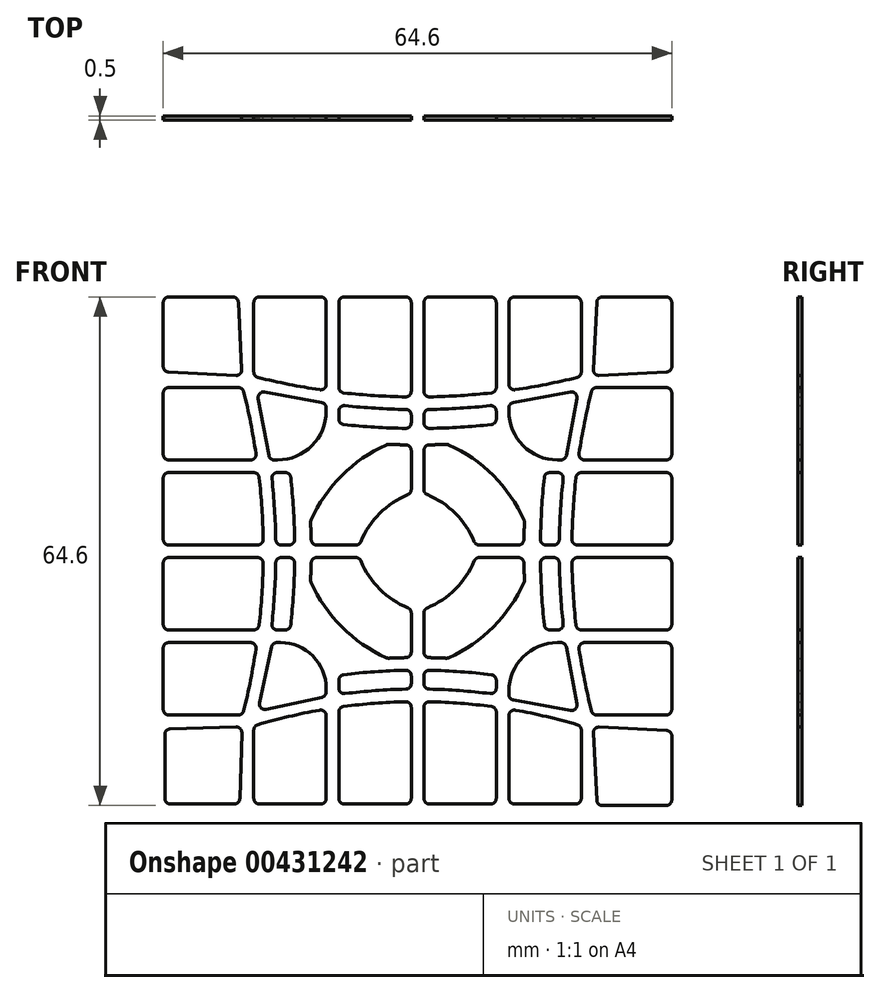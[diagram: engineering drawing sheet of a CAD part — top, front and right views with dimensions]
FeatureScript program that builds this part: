
annotation { "Feature Type Name" : "Feature", "Feature Type Description" : "" }
export const myFeature = defineFeature(function(context is Context, id is Id, definition is map)
    precondition{}
    {
        {
            var Q0;
            Q0=qCreatedBy(makeId("Front.planeOp"),FACE);
            var sketch = newSketch(context, id + "F0", { "sketchPlane" : qUnion([Q0])});
            skLineSegment(sketch, "E0.bottom", {"start": v(33.8, 33.8) * mm, "end": v(-33.8, 33.8) * mm, "construction": true});
            skLineSegment(sketch, "E0.top", {"start": v(33.8, -33.8) * mm, "end": v(-33.8, -33.8) * mm, "construction": true});
            skLineSegment(sketch, "E0.left", {"start": v(33.8, 33.8) * mm, "end": v(33.8, -33.8) * mm, "construction": true});
            skLineSegment(sketch, "E0.right", {"start": v(-33.8, 33.8) * mm, "end": v(-33.8, -33.8) * mm, "construction": true});
            skPoint(sketch, "E0.middle", {"position": v(0, 0) * mm});
            skLineSegment(sketch, "E1", {"start": v(0, 33.8) * mm, "end": v(0, -33.8) * mm, "construction": true});
            skLineSegment(sketch, "E2", {"start": v(-10.8, 33.8) * mm, "end": v(-10.8, -33.8) * mm, "construction": true});
            skLineSegment(sketch, "E3", {"start": v(-21.6, 33.8) * mm, "end": v(-21.6, -33.8) * mm, "construction": true});
            skLineSegment(sketch, "E4", {"start": v(-33.8, 0) * mm, "end": v(33.8, 0) * mm, "construction": true});
            skLineSegment(sketch, "E5", {"start": v(-33.8, -10.8) * mm, "end": v(33.8, -10.8) * mm, "construction": true});
            skLineSegment(sketch, "E6", {"start": v(-33.8, -21.6) * mm, "end": v(33.8, -21.6) * mm, "construction": true});
            skLineSegment(sketch, "E7", {"start": v(-33.8, -33.8) * mm, "end": v(0, 0) * mm});
            skLineSegment(sketch, "E8", {"start": v(-21.6, -33.8) * mm, "end": v(-21.2, -21.2) * mm, "construction": true});
            skLineSegment(sketch, "E9", {"start": v(-21.2, -21.2) * mm, "end": v(-33.8, -21.6) * mm, "construction": true});
            skLineSegment(sketch, "E10", {"start": v(-32.1, -31.4) * mm, "end": v(-32.1, -23.28) * mm});
            skLineSegment(sketch, "E11", {"start": v(-31.42, -22.58) * mm, "end": v(-23.04, -22.32) * mm});
            skLineSegment(sketch, "E12", {"start": v(-22.32, -23.04) * mm, "end": v(-22.58, -31.42) * mm});
            skLineSegment(sketch, "E13", {"start": v(-23.28, -32.1) * mm, "end": v(-31.4, -32.1) * mm});
            skPoint(sketch, "E14.visualSharp", {"position": v(-32.1, -22.6) * mm});
            skArc(sketch, "E14.filletArc", {"start": v(-31.42, -22.58) * mm, "mid": v(-31.9, -22.8) * mm, "end": v(-32.1, -23.28) * mm});
            skPoint(sketch, "E15.visualSharp", {"position": v(-22.3, -22.3) * mm});
            skArc(sketch, "E15.filletArc", {"start": v(-22.32, -23.04) * mm, "mid": v(-22.53, -22.53) * mm, "end": v(-23.04, -22.32) * mm});
            skPoint(sketch, "E16.visualSharp", {"position": v(-22.6, -32.1) * mm});
            skArc(sketch, "E16.filletArc", {"start": v(-23.28, -32.1) * mm, "mid": v(-22.8, -31.9) * mm, "end": v(-22.58, -31.42) * mm});
            skPoint(sketch, "E17.visualSharp", {"position": v(-32.1, -32.1) * mm});
            skArc(sketch, "E17.filletArc", {"start": v(-32.1, -31.4) * mm, "mid": v(-31.9, -31.9) * mm, "end": v(-31.4, -32.1) * mm});
            skLineSegment(sketch, "E18.MirrorCS", {"start": v(21.6, -33.8) * mm, "end": v(21.2, -21.2) * mm, "construction": true});
            skLineSegment(sketch, "E19", {"start": v(-20.8, -22.71) * mm, "end": v(-20.8, -31.4) * mm});
            skLineSegment(sketch, "E20", {"start": v(-20.1, -32.1) * mm, "end": v(-12.3, -32.1) * mm});
            skLineSegment(sketch, "E21", {"start": v(-11.6, -31.4) * mm, "end": v(-11.6, -20.88) * mm});
            skLineSegment(sketch, "E22", {"start": v(-10, -20.41) * mm, "end": v(-10, -31.4) * mm});
            skLineSegment(sketch, "E23", {"start": v(-9.3, -32.1) * mm, "end": v(-1.5, -32.1) * mm});
            skLineSegment(sketch, "E24", {"start": v(-0.8, -31.4) * mm, "end": v(-0.8, -19.82) * mm});
            skArc(sketch, "E25.trimOffspring", {"start": v(-12.42, -20.19) * mm, "mid": v(-16.39, -21) * mm, "end": v(-20.3, -22.04) * mm});
            skArc(sketch, "E26.trimOffspring", {"start": v(-1.51, -19.12) * mm, "mid": v(-5.46, -19.3) * mm, "end": v(-9.4, -19.72) * mm});
            skPoint(sketch, "E27.visualSharp", {"position": v(-20.8, -22.2) * mm});
            skArc(sketch, "E27.filletArc", {"start": v(-20.3, -22.04) * mm, "mid": v(-20.66, -22.3) * mm, "end": v(-20.8, -22.71) * mm});
            skPoint(sketch, "E28.visualSharp", {"position": v(-11.6, -20.05) * mm});
            skArc(sketch, "E28.filletArc", {"start": v(-11.6, -20.88) * mm, "mid": v(-11.85, -20.34) * mm, "end": v(-12.42, -20.19) * mm});
            skPoint(sketch, "E29.visualSharp", {"position": v(-11.6, -32.1) * mm});
            skArc(sketch, "E29.filletArc", {"start": v(-12.3, -32.1) * mm, "mid": v(-11.8, -31.9) * mm, "end": v(-11.6, -31.4) * mm});
            skPoint(sketch, "E30.visualSharp", {"position": v(-20.8, -32.1) * mm});
            skArc(sketch, "E30.filletArc", {"start": v(-20.8, -31.4) * mm, "mid": v(-20.6, -31.9) * mm, "end": v(-20.1, -32.1) * mm});
            skPoint(sketch, "E31.visualSharp", {"position": v(-10, -32.1) * mm});
            skArc(sketch, "E31.filletArc", {"start": v(-10, -31.4) * mm, "mid": v(-9.8, -31.9) * mm, "end": v(-9.3, -32.1) * mm});
            skPoint(sketch, "E32.visualSharp", {"position": v(-0.8, -32.1) * mm});
            skArc(sketch, "E32.filletArc", {"start": v(-1.5, -32.1) * mm, "mid": v(-1, -31.9) * mm, "end": v(-0.8, -31.4) * mm});
            skPoint(sketch, "E33.visualSharp", {"position": v(-0.8, -19.1) * mm});
            skArc(sketch, "E33.filletArc", {"start": v(-0.8, -19.82) * mm, "mid": v(-1.01, -19.32) * mm, "end": v(-1.51, -19.12) * mm});
            skPoint(sketch, "E34.visualSharp", {"position": v(-10, -19.8) * mm});
            skArc(sketch, "E34.filletArc", {"start": v(-9.4, -19.72) * mm, "mid": v(-9.83, -19.95) * mm, "end": v(-10, -20.41) * mm});
            skArc(sketch, "E35.0", {"start": v(17.07, -16.23) * mm, "mid": v(0, -14.3) * mm, "end": v(-17.07, -16.23) * mm, "construction": true});
            skLineSegment(sketch, "E36", {"start": v(-10, -17.39) * mm, "end": v(-10, -16.38) * mm});
            skLineSegment(sketch, "E37", {"start": v(-0.8, -15.82) * mm, "end": v(-0.8, -16.82) * mm});
            skArc(sketch, "E38", {"start": v(-1.51, -15.12) * mm, "mid": v(-5.46, -15.3) * mm, "end": v(-9.39, -15.69) * mm});
            skArc(sketch, "E39", {"start": v(-1.49, -17.52) * mm, "mid": v(-5.36, -17.7) * mm, "end": v(-9.21, -18.08) * mm});
            skPoint(sketch, "E40.visualSharp", {"position": v(-10, -18.19) * mm});
            skArc(sketch, "E40.filletArc", {"start": v(-10, -17.39) * mm, "mid": v(-9.76, -17.91) * mm, "end": v(-9.21, -18.08) * mm});
            skPoint(sketch, "E41.visualSharp", {"position": v(-10, -15.76) * mm});
            skArc(sketch, "E41.filletArc", {"start": v(-9.39, -15.69) * mm, "mid": v(-9.82, -15.92) * mm, "end": v(-10, -16.38) * mm});
            skPoint(sketch, "E42.visualSharp", {"position": v(-0.8, -15.1) * mm});
            skArc(sketch, "E42.filletArc", {"start": v(-0.8, -15.82) * mm, "mid": v(-1.01, -15.32) * mm, "end": v(-1.51, -15.12) * mm});
            skPoint(sketch, "E43.visualSharp", {"position": v(-0.8, -17.5) * mm});
            skArc(sketch, "E43.filletArc", {"start": v(-1.49, -17.52) * mm, "mid": v(-1, -17.3) * mm, "end": v(-0.8, -16.82) * mm});
            skLineSegment(sketch, "E44", {"start": v(-19.25, -20.08) * mm, "end": v(-12.15, -18.55) * mm});
            skLineSegment(sketch, "E45.MirrorCS", {"start": v(-20.08, -19.25) * mm, "end": v(-18.55, -12.15) * mm});
            skLineSegment(sketch, "E46", {"start": v(-11.6, -17.86) * mm, "end": v(-11.6, -17.43) * mm});
            skLineSegment(sketch, "E47.MirrorCS", {"start": v(-17.86, -11.6) * mm, "end": v(-17.43, -11.6) * mm});
            skArc(sketch, "E48", {"start": v(-11.6, -17.43) * mm, "mid": v(-13.3, -13.3) * mm, "end": v(-17.43, -11.6) * mm});
            skPoint(sketch, "E49.visualSharp", {"position": v(-18.43, -11.6) * mm});
            skArc(sketch, "E49.filletArc", {"start": v(-17.86, -11.6) * mm, "mid": v(-18.3, -11.76) * mm, "end": v(-18.55, -12.15) * mm});
            skPoint(sketch, "E50.visualSharp", {"position": v(-20.3, -20.3) * mm});
            skArc(sketch, "E50.filletArc", {"start": v(-20.08, -19.25) * mm, "mid": v(-19.89, -19.89) * mm, "end": v(-19.25, -20.08) * mm});
            skPoint(sketch, "E51.visualSharp", {"position": v(-11.6, -18.43) * mm});
            skArc(sketch, "E51.filletArc", {"start": v(-12.15, -18.55) * mm, "mid": v(-11.76, -18.3) * mm, "end": v(-11.6, -17.86) * mm});
            skCircle(sketch, "E52", {"center": v(0, 0) * mm, "radius": 6 * mm, "construction": true});
            skLineSegment(sketch, "E53", {"start": v(-0.8, -12.81) * mm, "end": v(-0.8, -7.84) * mm});
            skArc(sketch, "E54", {"start": v(-1.49, -13.51) * mm, "mid": v(-2.56, -13.54) * mm, "end": v(-3.63, -13.59) * mm});
            skArc(sketch, "E55.MirrorCS", {"start": v(-13.51, -1.49) * mm, "mid": v(-13.54, -2.56) * mm, "end": v(-13.59, -3.63) * mm});
            skLineSegment(sketch, "E56.MirrorCS", {"start": v(-12.81, -0.8) * mm, "end": v(-7.84, -0.8) * mm});
            skPoint(sketch, "E57.visualSharp", {"position": v(-13.6, -3.8) * mm});
            skPoint(sketch, "E58.visualSharp", {"position": v(-13.5, -0.8) * mm});
            skArc(sketch, "E58.filletArc", {"start": v(-12.81, -0.8) * mm, "mid": v(-13.3, -1) * mm, "end": v(-13.51, -1.49) * mm});
            skPoint(sketch, "E59.visualSharp", {"position": v(-7.36, -0.8) * mm});
            skPoint(sketch, "E60.visualSharp", {"position": v(-0.8, -7.36) * mm});
            skPoint(sketch, "E61.visualSharp", {"position": v(-0.8, -13.5) * mm});
            skArc(sketch, "E61.filletArc", {"start": v(-1.49, -13.51) * mm, "mid": v(-1, -13.3) * mm, "end": v(-0.8, -12.81) * mm});
            skPoint(sketch, "E62.visualSharp", {"position": v(-3.8, -13.6) * mm});
            skPoint(sketch, "E63.visualSharp", {"position": v(-9.62, -9.62) * mm});
            skLineSegment(sketch, "E64.MirrorCS", {"start": v(0.8, -31.4) * mm, "end": v(0.8, -19.82) * mm});
            skArc(sketch, "E65.MirrorCS", {"start": v(1.5, -32.1) * mm, "mid": v(1, -31.9) * mm, "end": v(0.8, -31.4) * mm});
            skLineSegment(sketch, "E66.MirrorCS", {"start": v(9.3, -32.1) * mm, "end": v(1.5, -32.1) * mm});
            skArc(sketch, "E67.MirrorCS", {"start": v(10, -31.4) * mm, "mid": v(9.8, -31.9) * mm, "end": v(9.3, -32.1) * mm});
            skLineSegment(sketch, "E68.MirrorCS", {"start": v(10, -20.41) * mm, "end": v(10, -31.4) * mm});
            skArc(sketch, "E69.MirrorCS", {"start": v(9.4, -19.72) * mm, "mid": v(9.83, -19.95) * mm, "end": v(10, -20.41) * mm});
            skArc(sketch, "E70.MirrorCS", {"start": v(1.51, -19.12) * mm, "mid": v(5.46, -19.3) * mm, "end": v(9.4, -19.72) * mm});
            skArc(sketch, "E71.MirrorCS", {"start": v(0.8, -19.82) * mm, "mid": v(1.01, -19.32) * mm, "end": v(1.51, -19.12) * mm});
            skArc(sketch, "E72.MirrorCS", {"start": v(11.6, -20.88) * mm, "mid": v(11.85, -20.34) * mm, "end": v(12.42, -20.19) * mm});
            skLineSegment(sketch, "E73.MirrorCS", {"start": v(11.6, -31.4) * mm, "end": v(11.6, -20.88) * mm});
            skArc(sketch, "E74.MirrorCS", {"start": v(12.3, -32.1) * mm, "mid": v(11.8, -31.9) * mm, "end": v(11.6, -31.4) * mm});
            skLineSegment(sketch, "E75.MirrorCS", {"start": v(20.1, -32.1) * mm, "end": v(12.3, -32.1) * mm});
            skArc(sketch, "E76.MirrorCS", {"start": v(20.8, -31.4) * mm, "mid": v(20.6, -31.9) * mm, "end": v(20.1, -32.1) * mm});
            skLineSegment(sketch, "E77.MirrorCS", {"start": v(20.8, -22.71) * mm, "end": v(20.8, -31.4) * mm});
            skArc(sketch, "E78.MirrorCS", {"start": v(20.3, -22.04) * mm, "mid": v(20.66, -22.3) * mm, "end": v(20.8, -22.71) * mm});
            skArc(sketch, "E79.MirrorCS", {"start": v(12.42, -20.19) * mm, "mid": v(16.39, -21) * mm, "end": v(20.3, -22.04) * mm});
            skArc(sketch, "E80.MirrorCS", {"start": v(1.51, -15.12) * mm, "mid": v(5.46, -15.3) * mm, "end": v(9.39, -15.69) * mm});
            skArc(sketch, "E81.MirrorCS", {"start": v(0.8, -15.82) * mm, "mid": v(1.01, -15.32) * mm, "end": v(1.51, -15.12) * mm});
            skLineSegment(sketch, "E82.MirrorCS", {"start": v(0.8, -15.82) * mm, "end": v(0.8, -16.82) * mm});
            skArc(sketch, "E83.MirrorCS", {"start": v(1.49, -17.52) * mm, "mid": v(1, -17.3) * mm, "end": v(0.8, -16.82) * mm});
            skArc(sketch, "E84.MirrorCS", {"start": v(1.49, -17.52) * mm, "mid": v(5.36, -17.7) * mm, "end": v(9.21, -18.08) * mm});
            skArc(sketch, "E85.MirrorCS", {"start": v(10, -17.39) * mm, "mid": v(9.76, -17.91) * mm, "end": v(9.21, -18.08) * mm});
            skLineSegment(sketch, "E86.MirrorCS", {"start": v(10, -17.39) * mm, "end": v(10, -16.38) * mm});
            skArc(sketch, "E87.MirrorCS", {"start": v(9.39, -15.69) * mm, "mid": v(9.82, -15.92) * mm, "end": v(10, -16.38) * mm});
            skLineSegment(sketch, "E88.1.0", {"start": v(31.6, -32.3) * mm, "end": v(23.47, -32.3) * mm});
            skArc(sketch, "E88.1.1", {"start": v(22.77, -31.63) * mm, "mid": v(22.98, -32.1) * mm, "end": v(23.47, -32.3) * mm});
            skLineSegment(sketch, "E88.1.2", {"start": v(22.77, -31.63) * mm, "end": v(22.34, -23.07) * mm});
            skArc(sketch, "E88.1.3", {"start": v(23.07, -22.34) * mm, "mid": v(22.54, -22.54) * mm, "end": v(22.34, -23.07) * mm});
            skLineSegment(sketch, "E88.1.4", {"start": v(23.07, -22.34) * mm, "end": v(31.63, -22.77) * mm});
            skArc(sketch, "E88.1.5", {"start": v(32.3, -23.47) * mm, "mid": v(32.1, -22.98) * mm, "end": v(31.63, -22.77) * mm});
            skLineSegment(sketch, "E88.1.6", {"start": v(32.3, -23.47) * mm, "end": v(32.3, -31.6) * mm});
            skArc(sketch, "E88.1.7", {"start": v(31.6, -32.3) * mm, "mid": v(32.1, -32.1) * mm, "end": v(32.3, -31.6) * mm});
            skLineSegment(sketch, "E88.1.8", {"start": v(22.76, -20.8) * mm, "end": v(31.6, -20.8) * mm});
            skArc(sketch, "E88.1.9", {"start": v(22.08, -20.27) * mm, "mid": v(22.33, -20.65) * mm, "end": v(22.76, -20.8) * mm});
            skArc(sketch, "E88.1.10", {"start": v(20.52, -12.4) * mm, "mid": v(21.2, -16.35) * mm, "end": v(22.08, -20.27) * mm});
            skArc(sketch, "E88.1.11", {"start": v(21.21, -11.6) * mm, "mid": v(20.68, -11.84) * mm, "end": v(20.52, -12.4) * mm});
            skLineSegment(sketch, "E88.1.12", {"start": v(31.6, -11.6) * mm, "end": v(21.21, -11.6) * mm});
            skArc(sketch, "E88.1.13", {"start": v(32.3, -12.3) * mm, "mid": v(32.1, -11.8) * mm, "end": v(31.6, -11.6) * mm});
            skLineSegment(sketch, "E88.1.14", {"start": v(32.3, -20.1) * mm, "end": v(32.3, -12.3) * mm});
            skArc(sketch, "E88.1.15", {"start": v(31.6, -20.8) * mm, "mid": v(32.1, -20.6) * mm, "end": v(32.3, -20.1) * mm});
            skArc(sketch, "E88.1.16", {"start": v(31.6, -10) * mm, "mid": v(32.1, -9.8) * mm, "end": v(32.3, -9.3) * mm});
            skLineSegment(sketch, "E88.1.17", {"start": v(20.82, -10) * mm, "end": v(31.6, -10) * mm});
            skArc(sketch, "E88.1.18", {"start": v(20.13, -9.38) * mm, "mid": v(20.35, -9.82) * mm, "end": v(20.82, -10) * mm});
            skArc(sketch, "E88.1.19", {"start": v(19.61, -1.51) * mm, "mid": v(19.78, -5.45) * mm, "end": v(20.13, -9.38) * mm});
            skArc(sketch, "E88.1.20", {"start": v(20.31, -0.8) * mm, "mid": v(19.81, -1) * mm, "end": v(19.61, -1.51) * mm});
            skLineSegment(sketch, "E88.1.21", {"start": v(31.6, -0.8) * mm, "end": v(20.31, -0.8) * mm});
            skArc(sketch, "E88.1.22", {"start": v(32.3, -1.5) * mm, "mid": v(32.1, -1) * mm, "end": v(31.6, -0.8) * mm});
            skLineSegment(sketch, "E88.1.23", {"start": v(32.3, -9.3) * mm, "end": v(32.3, -1.5) * mm});
            skArc(sketch, "E88.1.24", {"start": v(32.3, 1.5) * mm, "mid": v(32.1, 1) * mm, "end": v(31.6, 0.8) * mm});
            skLineSegment(sketch, "E88.1.25", {"start": v(32.3, 9.3) * mm, "end": v(32.3, 1.5) * mm});
            skArc(sketch, "E88.1.26", {"start": v(31.6, 10) * mm, "mid": v(32.1, 9.8) * mm, "end": v(32.3, 9.3) * mm});
            skLineSegment(sketch, "E88.1.27", {"start": v(20.82, 10) * mm, "end": v(31.6, 10) * mm});
            skArc(sketch, "E88.1.28", {"start": v(20.13, 9.38) * mm, "mid": v(20.35, 9.82) * mm, "end": v(20.82, 10) * mm});
            skArc(sketch, "E88.1.29", {"start": v(19.61, 1.51) * mm, "mid": v(19.78, 5.45) * mm, "end": v(20.13, 9.38) * mm});
            skArc(sketch, "E88.1.30", {"start": v(20.31, 0.8) * mm, "mid": v(19.81, 1) * mm, "end": v(19.61, 1.51) * mm});
            skLineSegment(sketch, "E88.1.31", {"start": v(31.6, 0.8) * mm, "end": v(20.31, 0.8) * mm});
            skArc(sketch, "E88.1.32", {"start": v(32.3, 12.3) * mm, "mid": v(32.1, 11.8) * mm, "end": v(31.6, 11.6) * mm});
            skLineSegment(sketch, "E88.1.33", {"start": v(32.3, 20.1) * mm, "end": v(32.3, 12.3) * mm});
            skArc(sketch, "E88.1.34", {"start": v(31.6, 20.8) * mm, "mid": v(32.1, 20.6) * mm, "end": v(32.3, 20.1) * mm});
            skLineSegment(sketch, "E88.1.35", {"start": v(22.76, 20.8) * mm, "end": v(31.6, 20.8) * mm});
            skArc(sketch, "E88.1.36", {"start": v(22.08, 20.27) * mm, "mid": v(22.33, 20.65) * mm, "end": v(22.76, 20.8) * mm});
            skArc(sketch, "E88.1.37", {"start": v(20.52, 12.4) * mm, "mid": v(21.2, 16.35) * mm, "end": v(22.08, 20.27) * mm});
            skArc(sketch, "E88.1.38", {"start": v(21.21, 11.6) * mm, "mid": v(20.68, 11.84) * mm, "end": v(20.52, 12.4) * mm});
            skLineSegment(sketch, "E88.1.39", {"start": v(31.6, 11.6) * mm, "end": v(21.21, 11.6) * mm});
            skArc(sketch, "E88.1.40", {"start": v(17.8, 10) * mm, "mid": v(18.32, 9.77) * mm, "end": v(18.5, 9.22) * mm});
            skArc(sketch, "E88.1.41", {"start": v(18.01, 1.49) * mm, "mid": v(18.17, 5.36) * mm, "end": v(18.5, 9.22) * mm});
            skArc(sketch, "E88.1.42", {"start": v(18.01, 1.49) * mm, "mid": v(17.8, 1) * mm, "end": v(17.31, 0.8) * mm});
            skLineSegment(sketch, "E88.1.43", {"start": v(16.31, 0.8) * mm, "end": v(17.31, 0.8) * mm});
            skArc(sketch, "E88.1.44", {"start": v(16.31, 0.8) * mm, "mid": v(15.81, 1) * mm, "end": v(15.61, 1.51) * mm});
            skArc(sketch, "E88.1.45", {"start": v(15.61, 1.51) * mm, "mid": v(15.77, 5.45) * mm, "end": v(16.1, 9.37) * mm});
            skArc(sketch, "E88.1.46", {"start": v(16.1, 9.37) * mm, "mid": v(16.33, 9.82) * mm, "end": v(16.8, 10) * mm});
            skLineSegment(sketch, "E88.1.47", {"start": v(17.8, 10) * mm, "end": v(16.8, 10) * mm});
            skArc(sketch, "E88.1.48", {"start": v(16.31, -0.8) * mm, "mid": v(15.81, -1) * mm, "end": v(15.61, -1.51) * mm});
            skArc(sketch, "E88.1.49", {"start": v(15.61, -1.51) * mm, "mid": v(15.77, -5.45) * mm, "end": v(16.1, -9.37) * mm});
            skLineSegment(sketch, "E88.1.50", {"start": v(16.31, -0.8) * mm, "end": v(17.31, -0.8) * mm});
            skArc(sketch, "E88.1.51", {"start": v(18.01, -1.49) * mm, "mid": v(17.8, -1) * mm, "end": v(17.31, -0.8) * mm});
            skArc(sketch, "E88.1.52", {"start": v(18.01, -1.49) * mm, "mid": v(18.17, -5.36) * mm, "end": v(18.5, -9.22) * mm});
            skArc(sketch, "E88.1.53", {"start": v(17.8, -10) * mm, "mid": v(18.32, -9.77) * mm, "end": v(18.5, -9.22) * mm});
            skLineSegment(sketch, "E88.1.54", {"start": v(17.8, -10) * mm, "end": v(16.8, -10) * mm});
            skArc(sketch, "E88.1.55", {"start": v(16.1, -9.37) * mm, "mid": v(16.33, -9.82) * mm, "end": v(16.8, -10) * mm});
            skArc(sketch, "E88.1.56", {"start": v(17.8, -11.6) * mm, "mid": v(13.41, -13.41) * mm, "end": v(11.6, -17.8) * mm});
            skLineSegment(sketch, "E88.1.57", {"start": v(18.2, -11.6) * mm, "end": v(17.8, -11.6) * mm});
            skArc(sketch, "E88.1.58", {"start": v(18.9, -12.17) * mm, "mid": v(18.66, -11.76) * mm, "end": v(18.2, -11.6) * mm});
            skLineSegment(sketch, "E88.1.59", {"start": v(20.23, -19.42) * mm, "end": v(18.9, -12.17) * mm});
            skArc(sketch, "E88.1.60", {"start": v(19.42, -20.23) * mm, "mid": v(20.04, -20.04) * mm, "end": v(20.23, -19.42) * mm});
            skLineSegment(sketch, "E88.1.61", {"start": v(19.42, -20.23) * mm, "end": v(12.17, -18.9) * mm});
            skArc(sketch, "E88.1.62", {"start": v(11.6, -18.2) * mm, "mid": v(11.76, -18.66) * mm, "end": v(12.17, -18.9) * mm});
            skLineSegment(sketch, "E88.1.63", {"start": v(11.6, -18.2) * mm, "end": v(11.6, -17.8) * mm});
            skLineSegment(sketch, "E88.2.0", {"start": v(32.3, 31.6) * mm, "end": v(32.3, 23.47) * mm});
            skArc(sketch, "E88.2.1", {"start": v(31.63, 22.77) * mm, "mid": v(32.1, 22.98) * mm, "end": v(32.3, 23.47) * mm});
            skLineSegment(sketch, "E88.2.2", {"start": v(31.63, 22.77) * mm, "end": v(23.07, 22.34) * mm});
            skArc(sketch, "E88.2.3", {"start": v(22.34, 23.07) * mm, "mid": v(22.54, 22.54) * mm, "end": v(23.07, 22.34) * mm});
            skLineSegment(sketch, "E88.2.4", {"start": v(22.34, 23.07) * mm, "end": v(22.77, 31.63) * mm});
            skArc(sketch, "E88.2.5", {"start": v(23.47, 32.3) * mm, "mid": v(22.98, 32.1) * mm, "end": v(22.77, 31.63) * mm});
            skLineSegment(sketch, "E88.2.6", {"start": v(23.47, 32.3) * mm, "end": v(31.6, 32.3) * mm});
            skArc(sketch, "E88.2.7", {"start": v(32.3, 31.6) * mm, "mid": v(32.1, 32.1) * mm, "end": v(31.6, 32.3) * mm});
            skLineSegment(sketch, "E88.2.8", {"start": v(20.8, 22.76) * mm, "end": v(20.8, 31.6) * mm});
            skArc(sketch, "E88.2.9", {"start": v(20.27, 22.08) * mm, "mid": v(20.65, 22.33) * mm, "end": v(20.8, 22.76) * mm});
            skArc(sketch, "E88.2.10", {"start": v(12.4, 20.52) * mm, "mid": v(16.35, 21.2) * mm, "end": v(20.27, 22.08) * mm});
            skArc(sketch, "E88.2.11", {"start": v(11.6, 21.21) * mm, "mid": v(11.84, 20.68) * mm, "end": v(12.4, 20.52) * mm});
            skLineSegment(sketch, "E88.2.12", {"start": v(11.6, 31.6) * mm, "end": v(11.6, 21.21) * mm});
            skArc(sketch, "E88.2.13", {"start": v(12.3, 32.3) * mm, "mid": v(11.8, 32.1) * mm, "end": v(11.6, 31.6) * mm});
            skLineSegment(sketch, "E88.2.14", {"start": v(20.1, 32.3) * mm, "end": v(12.3, 32.3) * mm});
            skArc(sketch, "E88.2.15", {"start": v(20.8, 31.6) * mm, "mid": v(20.6, 32.1) * mm, "end": v(20.1, 32.3) * mm});
            skArc(sketch, "E88.2.16", {"start": v(10, 31.6) * mm, "mid": v(9.8, 32.1) * mm, "end": v(9.3, 32.3) * mm});
            skLineSegment(sketch, "E88.2.17", {"start": v(10, 20.82) * mm, "end": v(10, 31.6) * mm});
            skArc(sketch, "E88.2.18", {"start": v(9.38, 20.13) * mm, "mid": v(9.82, 20.35) * mm, "end": v(10, 20.82) * mm});
            skArc(sketch, "E88.2.19", {"start": v(1.51, 19.61) * mm, "mid": v(5.45, 19.78) * mm, "end": v(9.38, 20.13) * mm});
            skArc(sketch, "E88.2.20", {"start": v(0.8, 20.31) * mm, "mid": v(1, 19.81) * mm, "end": v(1.51, 19.61) * mm});
            skLineSegment(sketch, "E88.2.21", {"start": v(0.8, 31.6) * mm, "end": v(0.8, 20.31) * mm});
            skArc(sketch, "E88.2.22", {"start": v(1.5, 32.3) * mm, "mid": v(1, 32.1) * mm, "end": v(0.8, 31.6) * mm});
            skLineSegment(sketch, "E88.2.23", {"start": v(9.3, 32.3) * mm, "end": v(1.5, 32.3) * mm});
            skArc(sketch, "E88.2.24", {"start": v(-1.5, 32.3) * mm, "mid": v(-1, 32.1) * mm, "end": v(-0.8, 31.6) * mm});
            skLineSegment(sketch, "E88.2.25", {"start": v(-9.3, 32.3) * mm, "end": v(-1.5, 32.3) * mm});
            skArc(sketch, "E88.2.26", {"start": v(-10, 31.6) * mm, "mid": v(-9.8, 32.1) * mm, "end": v(-9.3, 32.3) * mm});
            skLineSegment(sketch, "E88.2.27", {"start": v(-10, 20.82) * mm, "end": v(-10, 31.6) * mm});
            skArc(sketch, "E88.2.28", {"start": v(-9.38, 20.13) * mm, "mid": v(-9.82, 20.35) * mm, "end": v(-10, 20.82) * mm});
            skArc(sketch, "E88.2.29", {"start": v(-1.51, 19.61) * mm, "mid": v(-5.45, 19.78) * mm, "end": v(-9.38, 20.13) * mm});
            skArc(sketch, "E88.2.30", {"start": v(-0.8, 20.31) * mm, "mid": v(-1, 19.81) * mm, "end": v(-1.51, 19.61) * mm});
            skLineSegment(sketch, "E88.2.31", {"start": v(-0.8, 31.6) * mm, "end": v(-0.8, 20.31) * mm});
            skArc(sketch, "E88.2.32", {"start": v(-12.3, 32.3) * mm, "mid": v(-11.8, 32.1) * mm, "end": v(-11.6, 31.6) * mm});
            skLineSegment(sketch, "E88.2.33", {"start": v(-20.1, 32.3) * mm, "end": v(-12.3, 32.3) * mm});
            skArc(sketch, "E88.2.34", {"start": v(-20.8, 31.6) * mm, "mid": v(-20.6, 32.1) * mm, "end": v(-20.1, 32.3) * mm});
            skLineSegment(sketch, "E88.2.35", {"start": v(-20.8, 22.76) * mm, "end": v(-20.8, 31.6) * mm});
            skArc(sketch, "E88.2.36", {"start": v(-20.27, 22.08) * mm, "mid": v(-20.65, 22.33) * mm, "end": v(-20.8, 22.76) * mm});
            skArc(sketch, "E88.2.37", {"start": v(-12.4, 20.52) * mm, "mid": v(-16.35, 21.2) * mm, "end": v(-20.27, 22.08) * mm});
            skArc(sketch, "E88.2.38", {"start": v(-11.6, 21.21) * mm, "mid": v(-11.84, 20.68) * mm, "end": v(-12.4, 20.52) * mm});
            skLineSegment(sketch, "E88.2.39", {"start": v(-11.6, 31.6) * mm, "end": v(-11.6, 21.21) * mm});
            skArc(sketch, "E88.2.40", {"start": v(-10, 17.8) * mm, "mid": v(-9.77, 18.32) * mm, "end": v(-9.22, 18.5) * mm});
            skArc(sketch, "E88.2.41", {"start": v(-1.49, 18.01) * mm, "mid": v(-5.36, 18.17) * mm, "end": v(-9.22, 18.5) * mm});
            skArc(sketch, "E88.2.42", {"start": v(-1.49, 18.01) * mm, "mid": v(-1, 17.8) * mm, "end": v(-0.8, 17.31) * mm});
            skLineSegment(sketch, "E88.2.43", {"start": v(-0.8, 16.31) * mm, "end": v(-0.8, 17.31) * mm});
            skArc(sketch, "E88.2.44", {"start": v(-0.8, 16.31) * mm, "mid": v(-1, 15.81) * mm, "end": v(-1.51, 15.61) * mm});
            skArc(sketch, "E88.2.45", {"start": v(-1.51, 15.61) * mm, "mid": v(-5.45, 15.77) * mm, "end": v(-9.37, 16.1) * mm});
            skArc(sketch, "E88.2.46", {"start": v(-9.37, 16.1) * mm, "mid": v(-9.82, 16.33) * mm, "end": v(-10, 16.8) * mm});
            skLineSegment(sketch, "E88.2.47", {"start": v(-10, 17.8) * mm, "end": v(-10, 16.8) * mm});
            skArc(sketch, "E88.2.48", {"start": v(0.8, 16.31) * mm, "mid": v(1, 15.81) * mm, "end": v(1.51, 15.61) * mm});
            skArc(sketch, "E88.2.49", {"start": v(1.51, 15.61) * mm, "mid": v(5.45, 15.77) * mm, "end": v(9.37, 16.1) * mm});
            skLineSegment(sketch, "E88.2.50", {"start": v(0.8, 16.31) * mm, "end": v(0.8, 17.31) * mm});
            skArc(sketch, "E88.2.51", {"start": v(1.49, 18.01) * mm, "mid": v(1, 17.8) * mm, "end": v(0.8, 17.31) * mm});
            skArc(sketch, "E88.2.52", {"start": v(1.49, 18.01) * mm, "mid": v(5.36, 18.17) * mm, "end": v(9.22, 18.5) * mm});
            skArc(sketch, "E88.2.53", {"start": v(10, 17.8) * mm, "mid": v(9.77, 18.32) * mm, "end": v(9.22, 18.5) * mm});
            skLineSegment(sketch, "E88.2.54", {"start": v(10, 17.8) * mm, "end": v(10, 16.8) * mm});
            skArc(sketch, "E88.2.55", {"start": v(9.37, 16.1) * mm, "mid": v(9.82, 16.33) * mm, "end": v(10, 16.8) * mm});
            skArc(sketch, "E88.2.56", {"start": v(11.6, 17.8) * mm, "mid": v(13.41, 13.41) * mm, "end": v(17.8, 11.6) * mm});
            skLineSegment(sketch, "E88.2.57", {"start": v(11.6, 18.2) * mm, "end": v(11.6, 17.8) * mm});
            skArc(sketch, "E88.2.58", {"start": v(12.17, 18.9) * mm, "mid": v(11.76, 18.66) * mm, "end": v(11.6, 18.2) * mm});
            skLineSegment(sketch, "E88.2.59", {"start": v(19.42, 20.23) * mm, "end": v(12.17, 18.9) * mm});
            skArc(sketch, "E88.2.60", {"start": v(20.23, 19.42) * mm, "mid": v(20.04, 20.04) * mm, "end": v(19.42, 20.23) * mm});
            skLineSegment(sketch, "E88.2.61", {"start": v(20.23, 19.42) * mm, "end": v(18.9, 12.17) * mm});
            skArc(sketch, "E88.2.62", {"start": v(18.2, 11.6) * mm, "mid": v(18.66, 11.76) * mm, "end": v(18.9, 12.17) * mm});
            skLineSegment(sketch, "E88.2.63", {"start": v(18.2, 11.6) * mm, "end": v(17.8, 11.6) * mm});
            skLineSegment(sketch, "E88.3.0", {"start": v(-31.6, 32.3) * mm, "end": v(-23.47, 32.3) * mm});
            skArc(sketch, "E88.3.1", {"start": v(-22.77, 31.63) * mm, "mid": v(-22.98, 32.1) * mm, "end": v(-23.47, 32.3) * mm});
            skLineSegment(sketch, "E88.3.2", {"start": v(-22.77, 31.63) * mm, "end": v(-22.34, 23.07) * mm});
            skArc(sketch, "E88.3.3", {"start": v(-23.07, 22.34) * mm, "mid": v(-22.54, 22.54) * mm, "end": v(-22.34, 23.07) * mm});
            skLineSegment(sketch, "E88.3.4", {"start": v(-23.07, 22.34) * mm, "end": v(-31.63, 22.77) * mm});
            skArc(sketch, "E88.3.5", {"start": v(-32.3, 23.47) * mm, "mid": v(-32.1, 22.98) * mm, "end": v(-31.63, 22.77) * mm});
            skLineSegment(sketch, "E88.3.6", {"start": v(-32.3, 23.47) * mm, "end": v(-32.3, 31.6) * mm});
            skArc(sketch, "E88.3.7", {"start": v(-31.6, 32.3) * mm, "mid": v(-32.1, 32.1) * mm, "end": v(-32.3, 31.6) * mm});
            skLineSegment(sketch, "E88.3.8", {"start": v(-22.76, 20.8) * mm, "end": v(-31.6, 20.8) * mm});
            skArc(sketch, "E88.3.9", {"start": v(-22.08, 20.27) * mm, "mid": v(-22.33, 20.65) * mm, "end": v(-22.76, 20.8) * mm});
            skArc(sketch, "E88.3.10", {"start": v(-20.52, 12.4) * mm, "mid": v(-21.2, 16.35) * mm, "end": v(-22.08, 20.27) * mm});
            skArc(sketch, "E88.3.11", {"start": v(-21.21, 11.6) * mm, "mid": v(-20.68, 11.84) * mm, "end": v(-20.52, 12.4) * mm});
            skLineSegment(sketch, "E88.3.12", {"start": v(-31.6, 11.6) * mm, "end": v(-21.21, 11.6) * mm});
            skArc(sketch, "E88.3.13", {"start": v(-32.3, 12.3) * mm, "mid": v(-32.1, 11.8) * mm, "end": v(-31.6, 11.6) * mm});
            skLineSegment(sketch, "E88.3.14", {"start": v(-32.3, 20.1) * mm, "end": v(-32.3, 12.3) * mm});
            skArc(sketch, "E88.3.15", {"start": v(-31.6, 20.8) * mm, "mid": v(-32.1, 20.6) * mm, "end": v(-32.3, 20.1) * mm});
            skArc(sketch, "E88.3.16", {"start": v(-31.6, 10) * mm, "mid": v(-32.1, 9.8) * mm, "end": v(-32.3, 9.3) * mm});
            skLineSegment(sketch, "E88.3.17", {"start": v(-20.82, 10) * mm, "end": v(-31.6, 10) * mm});
            skArc(sketch, "E88.3.18", {"start": v(-20.13, 9.38) * mm, "mid": v(-20.35, 9.82) * mm, "end": v(-20.82, 10) * mm});
            skArc(sketch, "E88.3.19", {"start": v(-19.61, 1.51) * mm, "mid": v(-19.78, 5.45) * mm, "end": v(-20.13, 9.38) * mm});
            skArc(sketch, "E88.3.20", {"start": v(-20.31, 0.8) * mm, "mid": v(-19.81, 1) * mm, "end": v(-19.61, 1.51) * mm});
            skLineSegment(sketch, "E88.3.21", {"start": v(-31.6, 0.8) * mm, "end": v(-20.31, 0.8) * mm});
            skArc(sketch, "E88.3.22", {"start": v(-32.3, 1.5) * mm, "mid": v(-32.1, 1) * mm, "end": v(-31.6, 0.8) * mm});
            skLineSegment(sketch, "E88.3.23", {"start": v(-32.3, 9.3) * mm, "end": v(-32.3, 1.5) * mm});
            skArc(sketch, "E88.3.24", {"start": v(-32.3, -1.5) * mm, "mid": v(-32.1, -1) * mm, "end": v(-31.6, -0.8) * mm});
            skLineSegment(sketch, "E88.3.25", {"start": v(-32.3, -9.3) * mm, "end": v(-32.3, -1.5) * mm});
            skArc(sketch, "E88.3.26", {"start": v(-31.6, -10) * mm, "mid": v(-32.1, -9.8) * mm, "end": v(-32.3, -9.3) * mm});
            skLineSegment(sketch, "E88.3.27", {"start": v(-20.82, -10) * mm, "end": v(-31.6, -10) * mm});
            skArc(sketch, "E88.3.28", {"start": v(-20.13, -9.38) * mm, "mid": v(-20.35, -9.82) * mm, "end": v(-20.82, -10) * mm});
            skArc(sketch, "E88.3.29", {"start": v(-19.61, -1.51) * mm, "mid": v(-19.78, -5.45) * mm, "end": v(-20.13, -9.38) * mm});
            skArc(sketch, "E88.3.30", {"start": v(-20.31, -0.8) * mm, "mid": v(-19.81, -1) * mm, "end": v(-19.61, -1.51) * mm});
            skLineSegment(sketch, "E88.3.31", {"start": v(-31.6, -0.8) * mm, "end": v(-20.31, -0.8) * mm});
            skArc(sketch, "E88.3.32", {"start": v(-32.3, -12.3) * mm, "mid": v(-32.1, -11.8) * mm, "end": v(-31.6, -11.6) * mm});
            skLineSegment(sketch, "E88.3.33", {"start": v(-32.3, -20.1) * mm, "end": v(-32.3, -12.3) * mm});
            skArc(sketch, "E88.3.34", {"start": v(-31.6, -20.8) * mm, "mid": v(-32.1, -20.6) * mm, "end": v(-32.3, -20.1) * mm});
            skLineSegment(sketch, "E88.3.35", {"start": v(-22.76, -20.8) * mm, "end": v(-31.6, -20.8) * mm});
            skArc(sketch, "E88.3.36", {"start": v(-22.08, -20.27) * mm, "mid": v(-22.33, -20.65) * mm, "end": v(-22.76, -20.8) * mm});
            skArc(sketch, "E88.3.37", {"start": v(-20.52, -12.4) * mm, "mid": v(-21.2, -16.35) * mm, "end": v(-22.08, -20.27) * mm});
            skArc(sketch, "E88.3.38", {"start": v(-21.21, -11.6) * mm, "mid": v(-20.68, -11.84) * mm, "end": v(-20.52, -12.4) * mm});
            skLineSegment(sketch, "E88.3.39", {"start": v(-31.6, -11.6) * mm, "end": v(-21.21, -11.6) * mm});
            skArc(sketch, "E88.3.40", {"start": v(-17.8, -10) * mm, "mid": v(-18.32, -9.77) * mm, "end": v(-18.5, -9.22) * mm});
            skArc(sketch, "E88.3.41", {"start": v(-18.01, -1.49) * mm, "mid": v(-18.17, -5.36) * mm, "end": v(-18.5, -9.22) * mm});
            skArc(sketch, "E88.3.42", {"start": v(-18.01, -1.49) * mm, "mid": v(-17.8, -1) * mm, "end": v(-17.31, -0.8) * mm});
            skLineSegment(sketch, "E88.3.43", {"start": v(-16.31, -0.8) * mm, "end": v(-17.31, -0.8) * mm});
            skArc(sketch, "E88.3.44", {"start": v(-16.31, -0.8) * mm, "mid": v(-15.81, -1) * mm, "end": v(-15.61, -1.51) * mm});
            skArc(sketch, "E88.3.45", {"start": v(-15.61, -1.51) * mm, "mid": v(-15.77, -5.45) * mm, "end": v(-16.1, -9.37) * mm});
            skArc(sketch, "E88.3.46", {"start": v(-16.1, -9.37) * mm, "mid": v(-16.33, -9.82) * mm, "end": v(-16.8, -10) * mm});
            skLineSegment(sketch, "E88.3.47", {"start": v(-17.8, -10) * mm, "end": v(-16.8, -10) * mm});
            skArc(sketch, "E88.3.48", {"start": v(-16.31, 0.8) * mm, "mid": v(-15.81, 1) * mm, "end": v(-15.61, 1.51) * mm});
            skArc(sketch, "E88.3.49", {"start": v(-15.61, 1.51) * mm, "mid": v(-15.77, 5.45) * mm, "end": v(-16.1, 9.37) * mm});
            skLineSegment(sketch, "E88.3.50", {"start": v(-16.31, 0.8) * mm, "end": v(-17.31, 0.8) * mm});
            skArc(sketch, "E88.3.51", {"start": v(-18.01, 1.49) * mm, "mid": v(-17.8, 1) * mm, "end": v(-17.31, 0.8) * mm});
            skArc(sketch, "E88.3.52", {"start": v(-18.01, 1.49) * mm, "mid": v(-18.17, 5.36) * mm, "end": v(-18.5, 9.22) * mm});
            skArc(sketch, "E88.3.53", {"start": v(-17.8, 10) * mm, "mid": v(-18.32, 9.77) * mm, "end": v(-18.5, 9.22) * mm});
            skLineSegment(sketch, "E88.3.54", {"start": v(-17.8, 10) * mm, "end": v(-16.8, 10) * mm});
            skArc(sketch, "E88.3.55", {"start": v(-16.1, 9.37) * mm, "mid": v(-16.33, 9.82) * mm, "end": v(-16.8, 10) * mm});
            skArc(sketch, "E88.3.56", {"start": v(-17.8, 11.6) * mm, "mid": v(-13.41, 13.41) * mm, "end": v(-11.6, 17.8) * mm});
            skLineSegment(sketch, "E88.3.57", {"start": v(-18.2, 11.6) * mm, "end": v(-17.8, 11.6) * mm});
            skArc(sketch, "E88.3.58", {"start": v(-18.9, 12.17) * mm, "mid": v(-18.66, 11.76) * mm, "end": v(-18.2, 11.6) * mm});
            skLineSegment(sketch, "E88.3.59", {"start": v(-20.23, 19.42) * mm, "end": v(-18.9, 12.17) * mm});
            skArc(sketch, "E88.3.60", {"start": v(-19.42, 20.23) * mm, "mid": v(-20.04, 20.04) * mm, "end": v(-20.23, 19.42) * mm});
            skLineSegment(sketch, "E88.3.61", {"start": v(-19.42, 20.23) * mm, "end": v(-12.17, 18.9) * mm});
            skArc(sketch, "E88.3.62", {"start": v(-11.6, 18.2) * mm, "mid": v(-11.76, 18.66) * mm, "end": v(-12.17, 18.9) * mm});
            skLineSegment(sketch, "E88.3.63", {"start": v(-11.6, 18.2) * mm, "end": v(-11.6, 17.8) * mm});
            skLineSegment(sketch, "E89.MirrorCS", {"start": v(21.6, 33.8) * mm, "end": v(21.6, -33.8) * mm, "construction": true});
            skArc(sketch, "E90", {"start": v(21.6, -21.6) * mm, "mid": v(0, -18.3) * mm, "end": v(-21.6, -21.6) * mm, "construction": true});
            skArc(sketch, "E91", {"start": v(-13.52, -3.95) * mm, "mid": v(-9.62, -9.62) * mm, "end": v(-3.95, -13.52) * mm});
            skPoint(sketch, "E92.3.8", {"position": v(0.05, 7.55) * mm});
            skArc(sketch, "E93", {"start": v(-7.2, -1.23) * mm, "mid": v(-4.8, -4.8) * mm, "end": v(-1.23, -7.2) * mm});
            skArc(sketch, "E94.filletArc", {"start": v(-7.2, -1.23) * mm, "mid": v(-7.45, -0.92) * mm, "end": v(-7.84, -0.8) * mm});
            skArc(sketch, "E95.filletArc", {"start": v(-0.8, -7.84) * mm, "mid": v(-0.92, -7.45) * mm, "end": v(-1.23, -7.2) * mm});
            skArc(sketch, "E96.filletArc", {"start": v(-13.59, -3.63) * mm, "mid": v(-13.57, -3.8) * mm, "end": v(-13.52, -3.95) * mm});
            skArc(sketch, "E97.filletArc", {"start": v(-3.95, -13.52) * mm, "mid": v(-3.8, -13.57) * mm, "end": v(-3.63, -13.59) * mm});
            skPoint(sketch, "E98.1.0", {"position": v(0.8, -7.36) * mm});
            skLineSegment(sketch, "E98.1.1", {"start": v(0.8, -12.81) * mm, "end": v(0.8, -7.84) * mm});
            skArc(sketch, "E98.1.2", {"start": v(1.49, -13.51) * mm, "mid": v(2.56, -13.54) * mm, "end": v(3.63, -13.59) * mm});
            skPoint(sketch, "E98.1.3", {"position": v(9.62, -9.62) * mm});
            skPoint(sketch, "E98.1.4", {"position": v(0.8, -13.5) * mm});
            skPoint(sketch, "E98.1.5", {"position": v(3.8, -13.6) * mm});
            skPoint(sketch, "E98.1.6", {"position": v(0.8, -7.36) * mm});
            skArc(sketch, "E98.1.7", {"start": v(0.8, -12.81) * mm, "mid": v(1, -13.3) * mm, "end": v(1.49, -13.51) * mm});
            skPoint(sketch, "E98.1.8", {"position": v(3.8, -13.6) * mm});
            skArc(sketch, "E98.1.9", {"start": v(1.23, -7.2) * mm, "mid": v(0.92, -7.45) * mm, "end": v(0.8, -7.84) * mm});
            skArc(sketch, "E98.1.10", {"start": v(3.63, -13.59) * mm, "mid": v(3.8, -13.57) * mm, "end": v(3.95, -13.52) * mm});
            skArc(sketch, "E98.1.11", {"start": v(1.23, -7.2) * mm, "mid": v(4.8, -4.8) * mm, "end": v(7.2, -1.23) * mm});
            skArc(sketch, "E98.1.12", {"start": v(13.51, -1.49) * mm, "mid": v(13.54, -2.56) * mm, "end": v(13.59, -3.63) * mm});
            skPoint(sketch, "E98.1.13", {"position": v(13.5, -0.8) * mm});
            skLineSegment(sketch, "E98.1.14", {"start": v(12.81, -0.8) * mm, "end": v(7.84, -0.8) * mm});
            skPoint(sketch, "E98.1.15", {"position": v(7.36, -0.8) * mm});
            skPoint(sketch, "E98.1.16", {"position": v(13.6, -3.8) * mm});
            skArc(sketch, "E98.1.17", {"start": v(3.95, -13.52) * mm, "mid": v(9.62, -9.62) * mm, "end": v(13.52, -3.95) * mm});
            skArc(sketch, "E98.1.18", {"start": v(13.51, -1.49) * mm, "mid": v(13.3, -1) * mm, "end": v(12.81, -0.8) * mm});
            skPoint(sketch, "E98.1.19", {"position": v(7.36, -0.8) * mm});
            skPoint(sketch, "E98.1.20", {"position": v(13.6, -3.8) * mm});
            skArc(sketch, "E98.1.21", {"start": v(7.84, -0.8) * mm, "mid": v(7.45, -0.92) * mm, "end": v(7.2, -1.23) * mm});
            skArc(sketch, "E98.1.22", {"start": v(13.52, -3.95) * mm, "mid": v(13.57, -3.8) * mm, "end": v(13.59, -3.63) * mm});
            skPoint(sketch, "E98.2.0", {"position": v(7.36, 0.8) * mm});
            skLineSegment(sketch, "E98.2.1", {"start": v(12.81, 0.8) * mm, "end": v(7.84, 0.8) * mm});
            skArc(sketch, "E98.2.2", {"start": v(13.51, 1.49) * mm, "mid": v(13.54, 2.56) * mm, "end": v(13.59, 3.63) * mm});
            skPoint(sketch, "E98.2.3", {"position": v(9.62, 9.62) * mm});
            skPoint(sketch, "E98.2.4", {"position": v(13.5, 0.8) * mm});
            skPoint(sketch, "E98.2.5", {"position": v(13.6, 3.8) * mm});
            skPoint(sketch, "E98.2.6", {"position": v(7.36, 0.8) * mm});
            skArc(sketch, "E98.2.7", {"start": v(12.81, 0.8) * mm, "mid": v(13.3, 1) * mm, "end": v(13.51, 1.49) * mm});
            skPoint(sketch, "E98.2.8", {"position": v(13.6, 3.8) * mm});
            skArc(sketch, "E98.2.9", {"start": v(7.2, 1.23) * mm, "mid": v(7.45, 0.92) * mm, "end": v(7.84, 0.8) * mm});
            skArc(sketch, "E98.2.10", {"start": v(13.59, 3.63) * mm, "mid": v(13.57, 3.8) * mm, "end": v(13.52, 3.95) * mm});
            skArc(sketch, "E98.2.11", {"start": v(7.2, 1.23) * mm, "mid": v(4.8, 4.8) * mm, "end": v(1.23, 7.2) * mm});
            skArc(sketch, "E98.2.12", {"start": v(1.49, 13.51) * mm, "mid": v(2.56, 13.54) * mm, "end": v(3.63, 13.59) * mm});
            skPoint(sketch, "E98.2.13", {"position": v(0.8, 13.5) * mm});
            skLineSegment(sketch, "E98.2.14", {"start": v(0.8, 12.81) * mm, "end": v(0.8, 7.84) * mm});
            skPoint(sketch, "E98.2.15", {"position": v(0.8, 7.36) * mm});
            skPoint(sketch, "E98.2.16", {"position": v(3.8, 13.6) * mm});
            skArc(sketch, "E98.2.17", {"start": v(13.52, 3.95) * mm, "mid": v(9.62, 9.62) * mm, "end": v(3.95, 13.52) * mm});
            skArc(sketch, "E98.2.18", {"start": v(1.49, 13.51) * mm, "mid": v(1, 13.3) * mm, "end": v(0.8, 12.81) * mm});
            skPoint(sketch, "E98.2.19", {"position": v(0.8, 7.36) * mm});
            skPoint(sketch, "E98.2.20", {"position": v(3.8, 13.6) * mm});
            skArc(sketch, "E98.2.21", {"start": v(0.8, 7.84) * mm, "mid": v(0.92, 7.45) * mm, "end": v(1.23, 7.2) * mm});
            skArc(sketch, "E98.2.22", {"start": v(3.95, 13.52) * mm, "mid": v(3.8, 13.57) * mm, "end": v(3.63, 13.59) * mm});
            skPoint(sketch, "E98.3.0", {"position": v(-0.8, 7.36) * mm});
            skLineSegment(sketch, "E98.3.1", {"start": v(-0.8, 12.81) * mm, "end": v(-0.8, 7.84) * mm});
            skArc(sketch, "E98.3.2", {"start": v(-1.49, 13.51) * mm, "mid": v(-2.56, 13.54) * mm, "end": v(-3.63, 13.59) * mm});
            skPoint(sketch, "E98.3.3", {"position": v(-9.62, 9.62) * mm});
            skPoint(sketch, "E98.3.4", {"position": v(-0.8, 13.5) * mm});
            skPoint(sketch, "E98.3.5", {"position": v(-3.8, 13.6) * mm});
            skPoint(sketch, "E98.3.6", {"position": v(-0.8, 7.36) * mm});
            skArc(sketch, "E98.3.7", {"start": v(-0.8, 12.81) * mm, "mid": v(-1, 13.3) * mm, "end": v(-1.49, 13.51) * mm});
            skPoint(sketch, "E98.3.8", {"position": v(-3.8, 13.6) * mm});
            skArc(sketch, "E98.3.9", {"start": v(-1.23, 7.2) * mm, "mid": v(-0.92, 7.45) * mm, "end": v(-0.8, 7.84) * mm});
            skArc(sketch, "E98.3.10", {"start": v(-3.63, 13.59) * mm, "mid": v(-3.8, 13.57) * mm, "end": v(-3.95, 13.52) * mm});
            skArc(sketch, "E98.3.11", {"start": v(-1.23, 7.2) * mm, "mid": v(-4.8, 4.8) * mm, "end": v(-7.2, 1.23) * mm});
            skArc(sketch, "E98.3.12", {"start": v(-13.51, 1.49) * mm, "mid": v(-13.54, 2.56) * mm, "end": v(-13.59, 3.63) * mm});
            skPoint(sketch, "E98.3.13", {"position": v(-13.5, 0.8) * mm});
            skLineSegment(sketch, "E98.3.14", {"start": v(-12.81, 0.8) * mm, "end": v(-7.84, 0.8) * mm});
            skPoint(sketch, "E98.3.15", {"position": v(-7.36, 0.8) * mm});
            skPoint(sketch, "E98.3.16", {"position": v(-13.6, 3.8) * mm});
            skArc(sketch, "E98.3.17", {"start": v(-3.95, 13.52) * mm, "mid": v(-9.62, 9.62) * mm, "end": v(-13.52, 3.95) * mm});
            skArc(sketch, "E98.3.18", {"start": v(-13.51, 1.49) * mm, "mid": v(-13.3, 1) * mm, "end": v(-12.81, 0.8) * mm});
            skPoint(sketch, "E98.3.19", {"position": v(-7.36, 0.8) * mm});
            skPoint(sketch, "E98.3.20", {"position": v(-13.6, 3.8) * mm});
            skArc(sketch, "E98.3.21", {"start": v(-7.84, 0.8) * mm, "mid": v(-7.45, 0.92) * mm, "end": v(-7.2, 1.23) * mm});
            skArc(sketch, "E98.3.22", {"start": v(-13.52, 3.95) * mm, "mid": v(-13.57, 3.8) * mm, "end": v(-13.59, 3.63) * mm});
            skSolve(sketch);
        }
        {
            var Q0;
            Q0=qSketchRegion(id+"F0",true);
            extrude(context, id + "F1", {"entities" : qUnion([Q0]), "depth" : 0.5 * mm});
        }
    });
